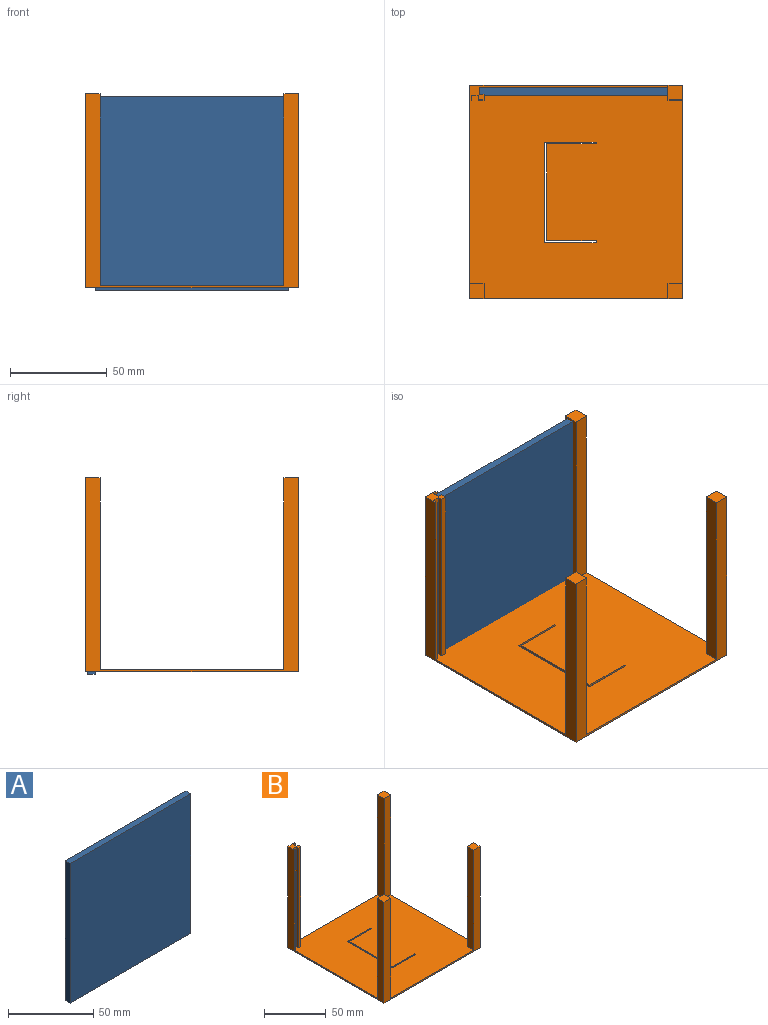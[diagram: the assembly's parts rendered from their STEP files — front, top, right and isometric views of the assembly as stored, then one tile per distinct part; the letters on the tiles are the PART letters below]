
ASSEMBLY  parts=2 mates=1
PART A: 6 faces, bbox 100x4x100 mm
  f0: plane 100x4mm, normal (-1,0,0), area 400mm2, adj f1,f3,f4,f5
  f1: plane 100x4mm, normal (0,0,-1), area 400mm2, adj f0,f2,f4,f5
  f2: plane 100x4mm, normal (1,0,0), area 400mm2, adj f1,f3,f4,f5
  f3: plane 100x4mm, normal (0,0,1), area 400mm2, adj f0,f2,f4,f5
  f4: plane 100x100mm, normal (0,-1,0), area 10000mm2, adj f0,f1,f2,f3
  f5: plane 100x100mm, normal (0,1,0), area 10000mm2, adj f0,f1,f2,f3
PART B: 34 faces, bbox 110x110x100 mm
  f0: plane 1.1x1mm, normal (-1,0,0), area 1.1mm2, adj f1,f11,f12,f13
  f1: plane 26.5x1mm, normal (0,1,0), area 26.5mm2, adj f0,f2,f12,f13
  f2: plane 52x1mm, normal (1,0,0), area 52mm2, adj f1,f3,f12,f13
  f3: plane 26.5x1mm, normal (0,-1,0), area 26.5mm2, adj f2,f4,f12,f13
  f4: plane 1x0.9mm, normal (-1,0,0), area 0.9mm2, adj f3,f5,f12,f13
  f5: plane 25.34x1mm, normal (0,1,0), area 25.3mm2, adj f4,f6,f12,f13
  f6: plane 50x1mm, normal (-1,0,0), area 50mm2, adj f5,f11,f12,f13
  f7: plane 110x100mm, normal (0,1,0), area 1595mm2, adj f8,f10,f12,f13,f14,f24,f29,f30
  f8: plane 110x100mm, normal (-1,0,0), area 1595mm2, adj f7,f9,f12,f13,f15,f24,f26,f27
  f9: plane 110x100mm, normal (0,-1,0), area 1595mm2, adj f8,f10,f12,f13,f25,f27,f31,f33
  f10: plane 110x100mm, normal (1,0,0), area 1595mm2, adj f7,f9,f12,f13,f28,f30,f32,f33
  f11: plane 25.34x1mm, normal (0,-1,0), area 25.3mm2, adj f0,f6,f12,f13
  f12: plane 110x110mm, normal (0,0,1), area 11781.5mm2, adj f0,f1,f2,f3,f4,f5,f6,f7
  f13: plane 110x110mm, normal (0,0,-1), area 11989mm2, adj f0,f1,f2,f3,f4,f5,f6,f7
  f14: plane 99x1mm, normal (1,0,0), area 99mm2, adj f7,f12,f23,f24
  f15: plane 99x1mm, normal (0,-1,0), area 99mm2, adj f8,f12,f16,f24
  f16: plane 99x2.5mm, normal (1,0,0), area 247.5mm2, adj f12,f15,f17,f24
  f17: plane 99x3.5mm, normal (0,-1,0), area 346.5mm2, adj f12,f16,f18,f24
  f18: plane 99x2.5mm, normal (-1,0,0), area 247.5mm2, adj f12,f17,f19,f24
  f19: plane 99x3mm, normal (0,-1,0), area 297mm2, adj f12,f18,f20,f24
  f20: plane 99x3mm, normal (1,0,0), area 297mm2, adj f12,f19,f21,f24
  f21: plane 99x2.5mm, normal (0,1,0), area 247.5mm2, adj f12,f20,f22,f24
  f22: plane 99x3.5mm, normal (1,0,0), area 346.5mm2, adj f12,f21,f23,f24
  f23: plane 99x2.5mm, normal (0,-1,0), area 247.5mm2, adj f12,f14,f22,f24
  f24: plane 7.5x7.5mm, normal (0,0,1), area 38.7mm2, adj f7,f8,f14,f15,f16,f17,f18,f19
  f25: plane 99x7.5mm, normal (1,0,0), area 742.5mm2, adj f9,f12,f26,f27
  f26: plane 99x7.5mm, normal (0,1,0), area 742.5mm2, adj f8,f12,f25,f27
  f27: plane 7.5x7.5mm, normal (0,0,1), area 56.2mm2, adj f8,f9,f25,f26
  f28: plane 99x7.5mm, normal (0,-1,0), area 742.5mm2, adj f10,f12,f29,f30
  f29: plane 99x7.5mm, normal (-1,0,0), area 742.5mm2, adj f7,f12,f28,f30
  f30: plane 7.5x7.5mm, normal (0,0,1), area 56.2mm2, adj f7,f10,f28,f29
  f31: plane 99x7.5mm, normal (-1,0,0), area 742.5mm2, adj f9,f12,f32,f33
  f32: plane 99x7.5mm, normal (0,1,0), area 742.5mm2, adj f10,f12,f31,f33
  f33: plane 7.5x7.5mm, normal (0,0,1), area 56.2mm2, adj f9,f10,f31,f32
PLACE A t=(-51.12,58.52,42.16)mm
PLACE B t=(-49.52,4.52,-15.23)mm fixed
MATE slider A.f1 <-> B.f12  axis (0,0,1) through (-99.52,58.52,-1.64)mm
